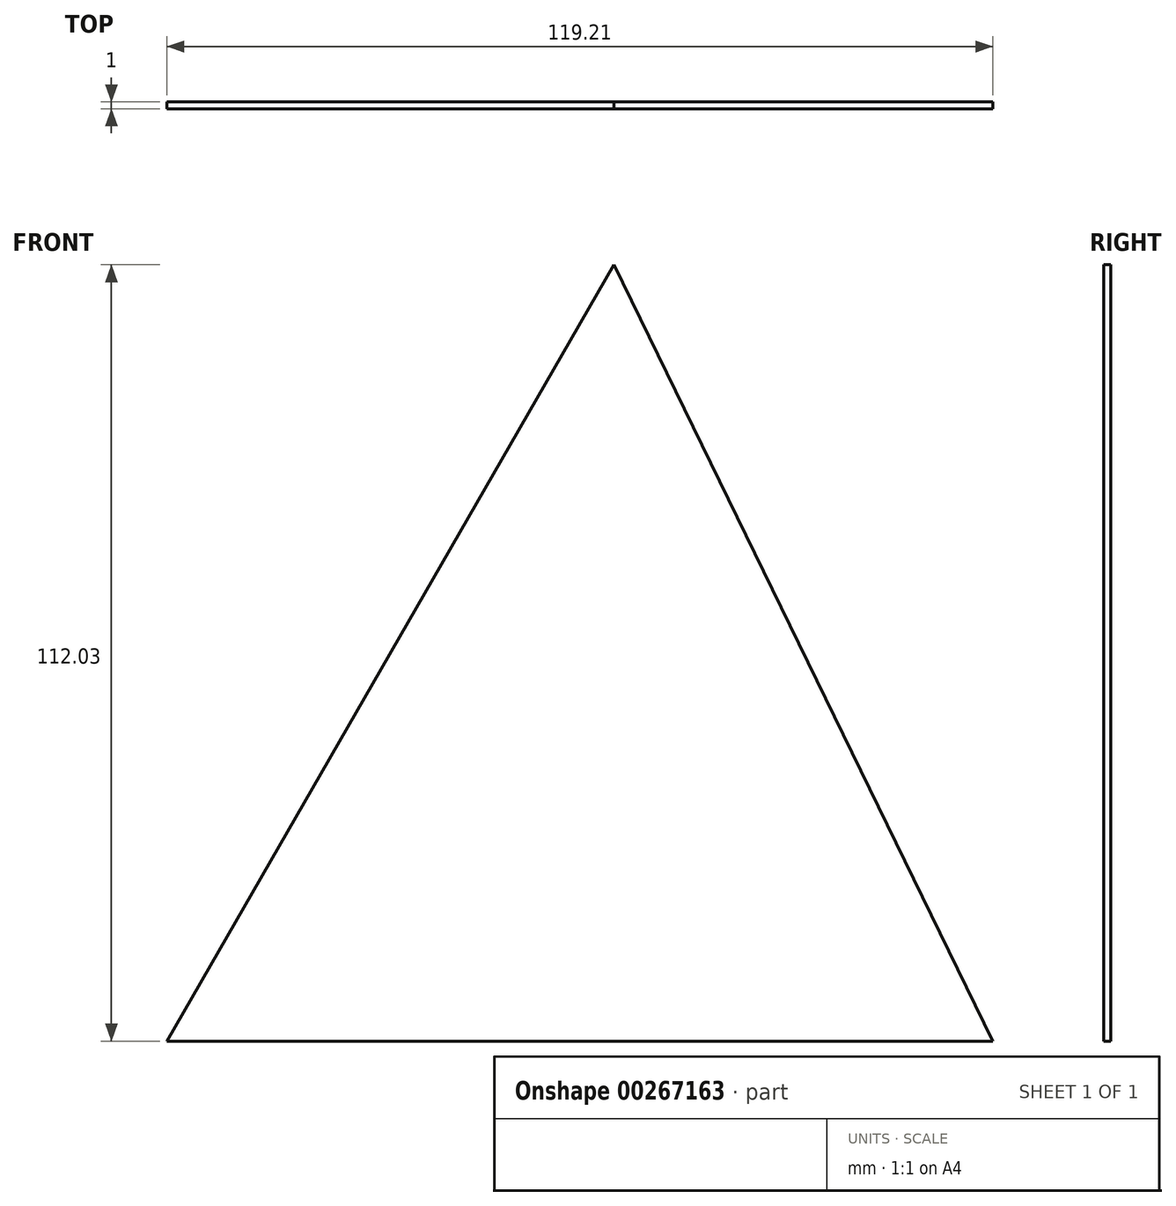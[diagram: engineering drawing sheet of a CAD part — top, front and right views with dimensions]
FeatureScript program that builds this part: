
annotation { "Feature Type Name" : "Feature", "Feature Type Description" : "" }
export const myFeature = defineFeature(function(context is Context, id is Id, definition is map)
    precondition{}
    {
        {
            var Q0;
            Q0=qCreatedBy(makeId("Front.planeOp"),FACE);
            var sketch = newSketch(context, id + "F0", { "sketchPlane" : qUnion([Q0])});
            skLineSegment(sketch, "E0", {"start": v(5.39, 63.29) * mm, "end": v(-59.1, -48.74) * mm});
            skLineSegment(sketch, "E1", {"start": v(-59.1, -48.74) * mm, "end": v(60.1, -48.74) * mm});
            skLineSegment(sketch, "E2", {"start": v(60.1, -48.74) * mm, "end": v(5.39, 63.29) * mm});
            skSolve(sketch);
        }
        {
            var Q0;
            Q0=makeQuery(id+"F0.imprint","IMPRINT",FACE,{"disambiguationData":[TD([[makeQuery(id+"F0.imprint","IMPRINT",EDGE,{"derivedFrom":sQuery(id+"F0.wireOp",EDGE,"E0")}),1.0]])]});
            extrude(context, id + "F1", {"entities" : qUnion([Q0]), "depth" : 1 * mm});
        }
    });
